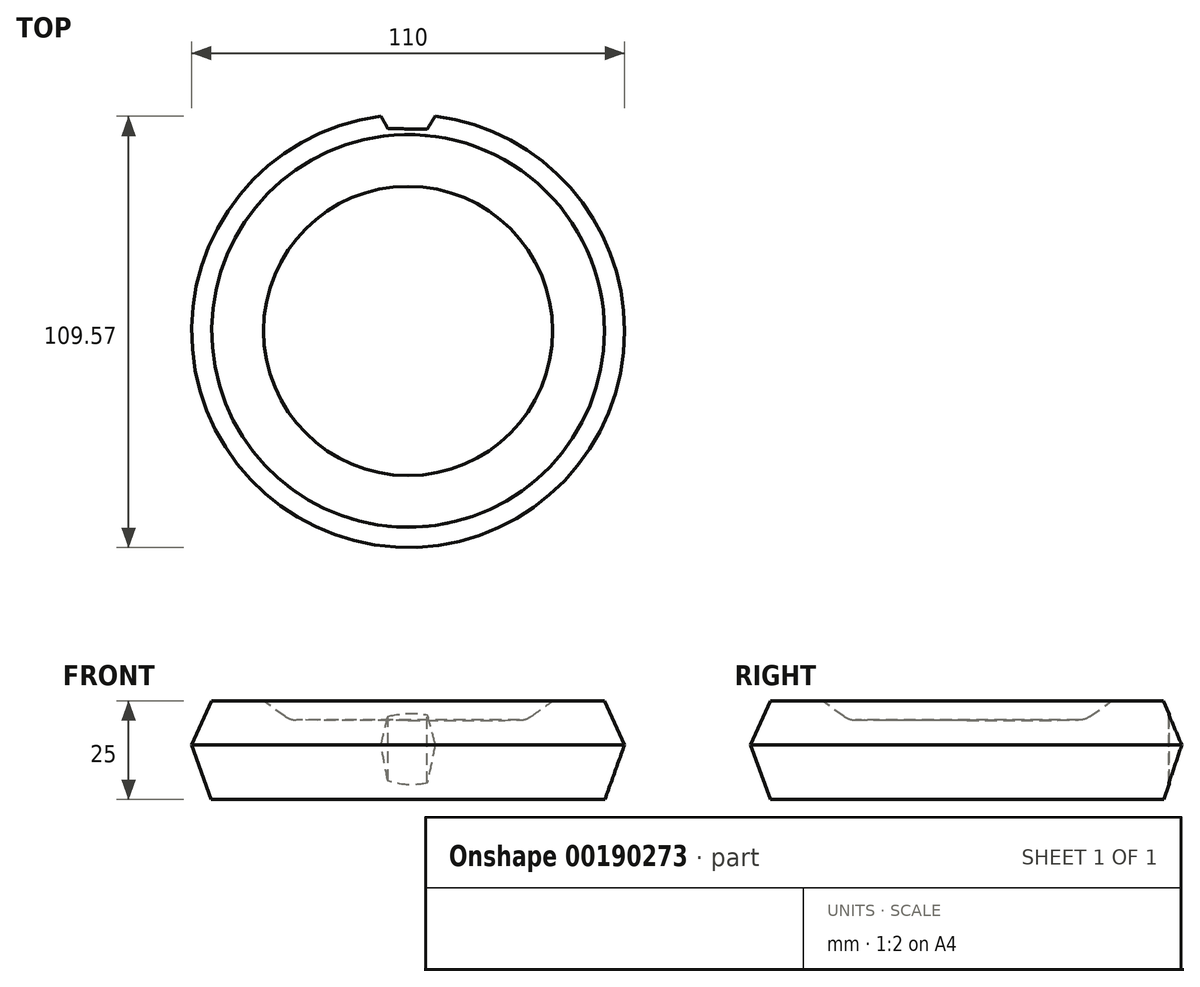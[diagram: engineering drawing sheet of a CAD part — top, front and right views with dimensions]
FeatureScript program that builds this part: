
annotation { "Feature Type Name" : "Feature", "Feature Type Description" : "" }
export const myFeature = defineFeature(function(context is Context, id is Id, definition is map)
    precondition{}
    {
        {
            var Q0;
            Q0=qCreatedBy(makeId("Front.planeOp"),FACE);
            var sketch = newSketch(context, id + "F0", { "sketchPlane" : qUnion([Q0])});
            skLineSegment(sketch, "E0.0", {"start": v(-36.74, 24.94) * mm, "end": v(-29.92, 20.13) * mm});
            skLineSegment(sketch, "E0.3", {"start": v(-50, 0) * mm, "end": v(-55, 13.82) * mm});
            skLineSegment(sketch, "E0.4", {"start": v(-55, 13.82) * mm, "end": v(-49.88, 25) * mm});
            skLineSegment(sketch, "E0.5", {"start": v(-49.88, 25) * mm, "end": v(-36.74, 24.94) * mm});
            skPoint(sketch, "E0.0.midPoint", {"position": v(-29.92, 20.13) * mm});
            skLineSegment(sketch, "E1", {"start": v(0, 0) * mm, "end": v(-50, 0) * mm});
            skLineSegment(sketch, "E2", {"start": v(-29.92, 20.13) * mm, "end": v(0, 20) * mm});
            skLineSegment(sketch, "E3", {"start": v(0, 20) * mm, "end": v(0, 0) * mm});
            skPoint(sketch, "E4.orphan", {"position": v(-23.11, 15.33) * mm});
            skPoint(sketch, "E5.orphan", {"position": v(-34, 4) * mm});
            skSolve(sketch);
        }
        {
            var Q0;
            Q0=makeQuery(id+"F0.imprint","IMPRINT",FACE,{"disambiguationData":[TD([[makeQuery(id+"F0.imprint","IMPRINT",EDGE,{"derivedFrom":sQuery(id+"F0.wireOp",EDGE,"E0.0")}),-1.0]])]});
            var Q1;
            Q1=sQuery(id+"F0.wireOp",EDGE,"E3");
            revolve(context, id + "F1", {"entities" : qUnion([Q0]), "axis" : qUnion([Q1]), "revolveType" : RevolveType.FULL});
        }
        {
            var Q0;
            Q0=makeQuery(id+"F1.opRevolve","SWEPT_EDGE",EDGE,{"disambiguationData":[OSD([sQuery(id+"F0.wireOp",EDGE,"E0.0"),sQuery(id+"F0.wireOp",EDGE,"E2")])]});
            fillet(context, id + "F2", {"entities" : qUnion([Q0]), "radius" : 5 * mm, "tangentPropagation" : true, "allowEdgeOverflow" : false});
        }
        {
            var Q0;
            Q0=qCreatedBy(makeId("Top.planeOp"),FACE);
            cPlane(context, id + "F3", {"entities" : qUnion([Q0]), "cplaneType" : CPlaneType.OFFSET, "offset" : 25 * mm, "width" : 150 * mm, "height" : 150 * mm});
        }
        {
            var Q0;
            Q0=qCreatedBy(id+"F3.planeOp",FACE);
            var sketch = newSketch(context, id + "F4", { "sketchPlane" : qUnion([Q0])});
            skCircle(sketch, "E6.cCircle", {"center": v(0, 60) * mm, "radius": 8.66 * mm, "construction": true});
            skLineSegment(sketch, "E6.0", {"start": v(5.14, 68.58) * mm, "end": v(10, 59.84) * mm});
            skLineSegment(sketch, "E6.1", {"start": v(10, 59.84) * mm, "end": v(4.86, 51.26) * mm});
            skLineSegment(sketch, "E6.2", {"start": v(4.86, 51.26) * mm, "end": v(-5.14, 51.42) * mm});
            skLineSegment(sketch, "E6.3", {"start": v(-5.14, 51.42) * mm, "end": v(-10, 60.16) * mm});
            skLineSegment(sketch, "E6.4", {"start": v(-10, 60.16) * mm, "end": v(-4.86, 68.74) * mm});
            skLineSegment(sketch, "E6.5", {"start": v(-4.86, 68.74) * mm, "end": v(5.14, 68.58) * mm});
            skPoint(sketch, "E6.0.midPoint", {"position": v(7.57, 64.2) * mm});
            skSolve(sketch);
        }
        {
            var Q0;
            Q0=makeQuery(id+"F4.imprint","IMPRINT",FACE,{"disambiguationData":[TD([[makeQuery(id+"F4.imprint","IMPRINT",EDGE,{"derivedFrom":sQuery(id+"F4.wireOp",EDGE,"E6.0")}),-1.0]])]});
            extrude(context, id + "F5", {"entities" : qUnion([Q0]), "operationType" : NewBodyOperationType.REMOVE, "oppositeDirection" : true, "depth" : 25 * mm});
        }
    });
